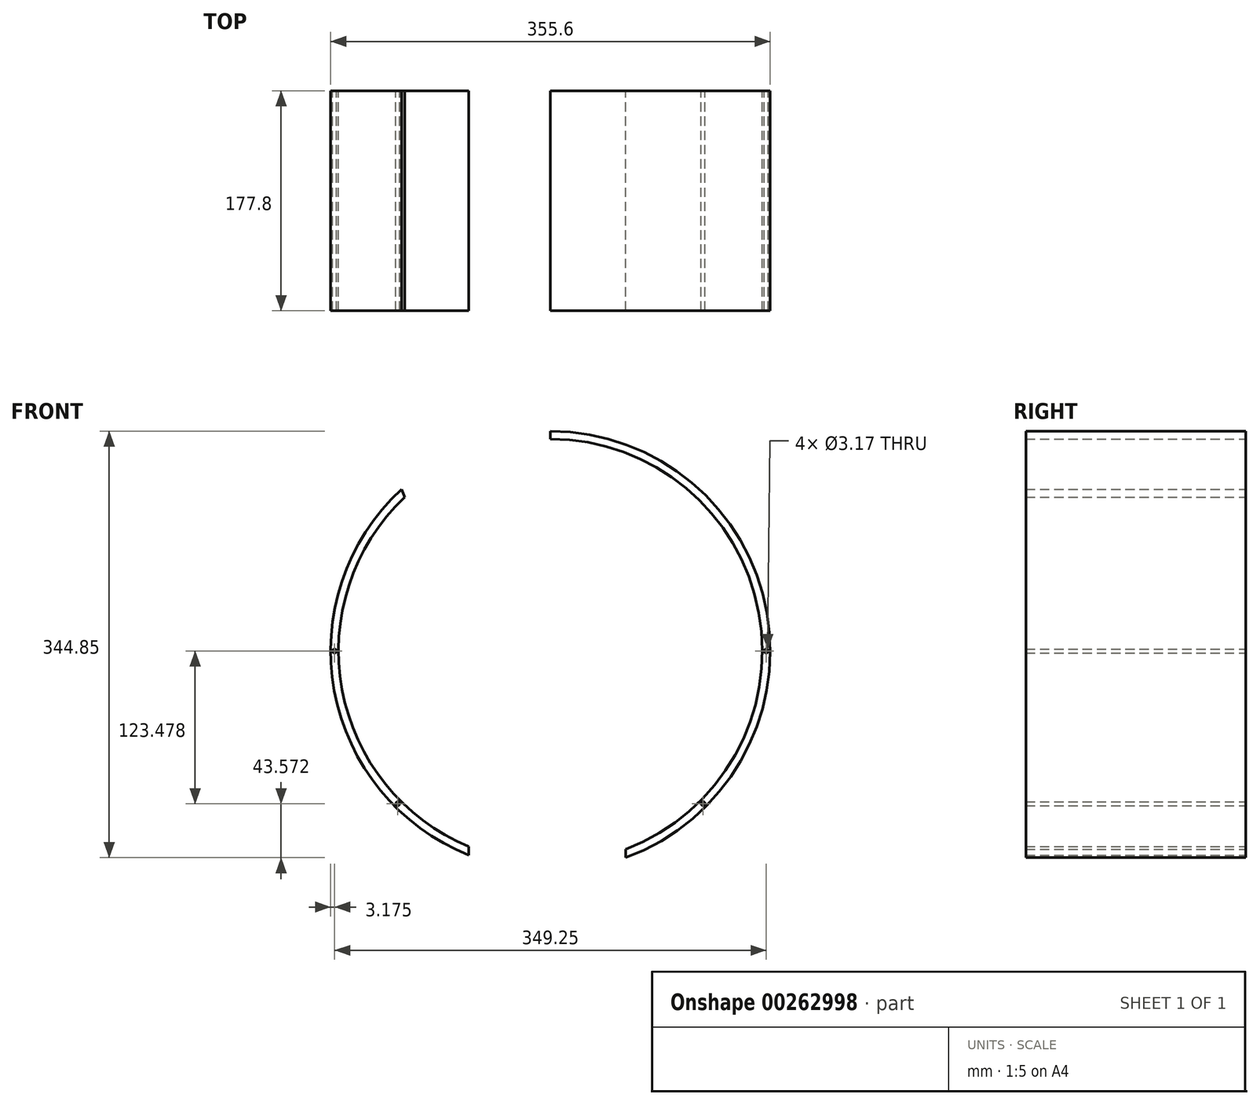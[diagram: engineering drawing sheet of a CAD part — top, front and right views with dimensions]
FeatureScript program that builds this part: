
annotation { "Feature Type Name" : "Feature", "Feature Type Description" : "" }
export const myFeature = defineFeature(function(context is Context, id is Id, definition is map)
    precondition{}
    {
        {
            var Q0;
            Q0=qCreatedBy(makeId("Front.planeOp"),FACE);
            var sketch = newSketch(context, id + "F0", { "sketchPlane" : qUnion([Q0])});
            skArc(sketch, "E0", {"start": v(60.9, -167.05) * mm, "mid": v(175.1, 30.92) * mm, "end": v(0, 177.8) * mm});
            skArc(sketch, "E1", {"start": v(60.9, -160.27) * mm, "mid": v(168.63, 30.96) * mm, "end": v(0, 171.45) * mm});
            skLineSegment(sketch, "E2", {"start": v(-66.08, -158.2) * mm, "end": v(-66.08, -165.06) * mm});
            skLineSegment(sketch, "E3", {"start": v(60.9, -160.27) * mm, "end": v(60.9, -167.05) * mm});
            skLineSegment(sketch, "E4", {"start": v(-117.97, 124.41) * mm, "end": v(-120.5, 130.75) * mm});
            skLineSegment(sketch, "E5", {"start": v(0, 171.45) * mm, "end": v(0, 177.8) * mm});
            skArc(sketch, "E6.trimOffspring", {"start": v(-120.5, 130.75) * mm, "mid": v(-174.87, -32.16) * mm, "end": v(-66.08, -165.06) * mm});
            skArc(sketch, "E7.trimOffspring", {"start": v(-117.97, 124.41) * mm, "mid": v(-168.63, -30.96) * mm, "end": v(-66.08, -158.2) * mm});
            skCircle(sketch, "E8", {"center": v(174.62, 0) * mm, "radius": 1.59 * mm});
            skCircle(sketch, "E9", {"center": v(-174.62, 0) * mm, "radius": 1.59 * mm});
            skCircle(sketch, "E10", {"center": v(-123.48, -123.48) * mm, "radius": 1.59 * mm});
            skCircle(sketch, "E11", {"center": v(123.48, -123.48) * mm, "radius": 1.59 * mm});
            skSolve(sketch);
        }
        {
            var Q0;
            Q0=makeQuery(id+"F0.imprint","IMPRINT",FACE,{"disambiguationData":[TD([[makeQuery(id+"F0.imprint","IMPRINT",EDGE,{"derivedFrom":sQuery(id+"F0.wireOp",EDGE,"E2")}),-1.0]])]});
            var Q1;
            Q1=makeQuery(id+"F0.imprint","IMPRINT",FACE,{"disambiguationData":[TD([[makeQuery(id+"F0.imprint","IMPRINT",EDGE,{"derivedFrom":sQuery(id+"F0.wireOp",EDGE,"E0")}),1.0]])]});
            extrude(context, id + "F1", {"entities" : qUnion([Q0, Q1]), "depth" : 177.8 * mm});
        }
    });
